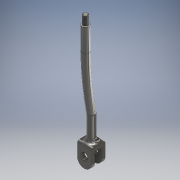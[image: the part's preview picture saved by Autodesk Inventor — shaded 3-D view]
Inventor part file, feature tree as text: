
AUTODESK INVENTOR PART (.ipt)
format: ipt  version: 2017 (Build 210142000, 142)  size: 204,288 bytes
history: native  units: mm
features: sketch x5, extrude x3, fillet x3, sweep x1, chamfer x1, thread x1, plane x1, projected_geometry x1
ambient origin geometry x8: Origin, YZ Plane, XZ Plane, XY Plane, X Axis, Y Axis, Z Axis, Center Point
bodies: Solid1 (feature_tree)
feature tree (16):
  sweep  "Sweep1"
  extrude  "Extrusion1"  Depth=2.05mm
  chamfer  "Chamfer1"  Distance=4.0mm
  thread  "Thread1"  [1 undecoded]
  plane  "Work Plane1"
  extrude  "Extrusion2"  TaperAngle=0.0deg  [1 undecoded]
  extrude  "Extrusion3"  Depth=6.0mm TaperAngle=0.0deg
  fillet  "Fillet1"  Radius=3.0mm
  fillet  "Fillet2"  [1 undecoded]
  fillet  "Fillet3"  Radius=3.0mm
  sketch  "Sketch1"  dims[d0=10.0mm d1=2.5mm d2=100.0mm d3=3.0mm]
  sketch  "Sketch2"  dims[d4=0.0mm d5=0.0mm d6=2.05mm d7=4.0mm d8=0.0mm d9=0.25mm d10=2.0mm d11=45.0deg]
  sketch  "Sketch3"  dims[d12=10.0mm d13=0.0mm d14=0.0mm]
  sketch  "Sketch6"  dims[d15=3.0mm d16=6.0mm d17=0.0mm d20=3.0mm d21=0.0mm d22=0.0mm d23=3.0mm]
  sketch  "Sketch7"  dims[d24=1.5mm d25=1.0mm d28=90.0deg d29=1.5mm d30=4.5mm d31=6.0mm d32=9.0mm d33=7.0mm d34=0.0mm d35=3.0mm d36=1.5mm d37=3.0mm d38=51.0mm d39=3.0mm d40=2.5mm d41=3.0mm d42=4.5mm]
  projected_geometry  "Projected Loop1"
note: 3 required parameter values undecoded (feature->parameter linkage not recoverable at this tier; creation-order binding heuristic only, values carry confidence <= 0.55)
